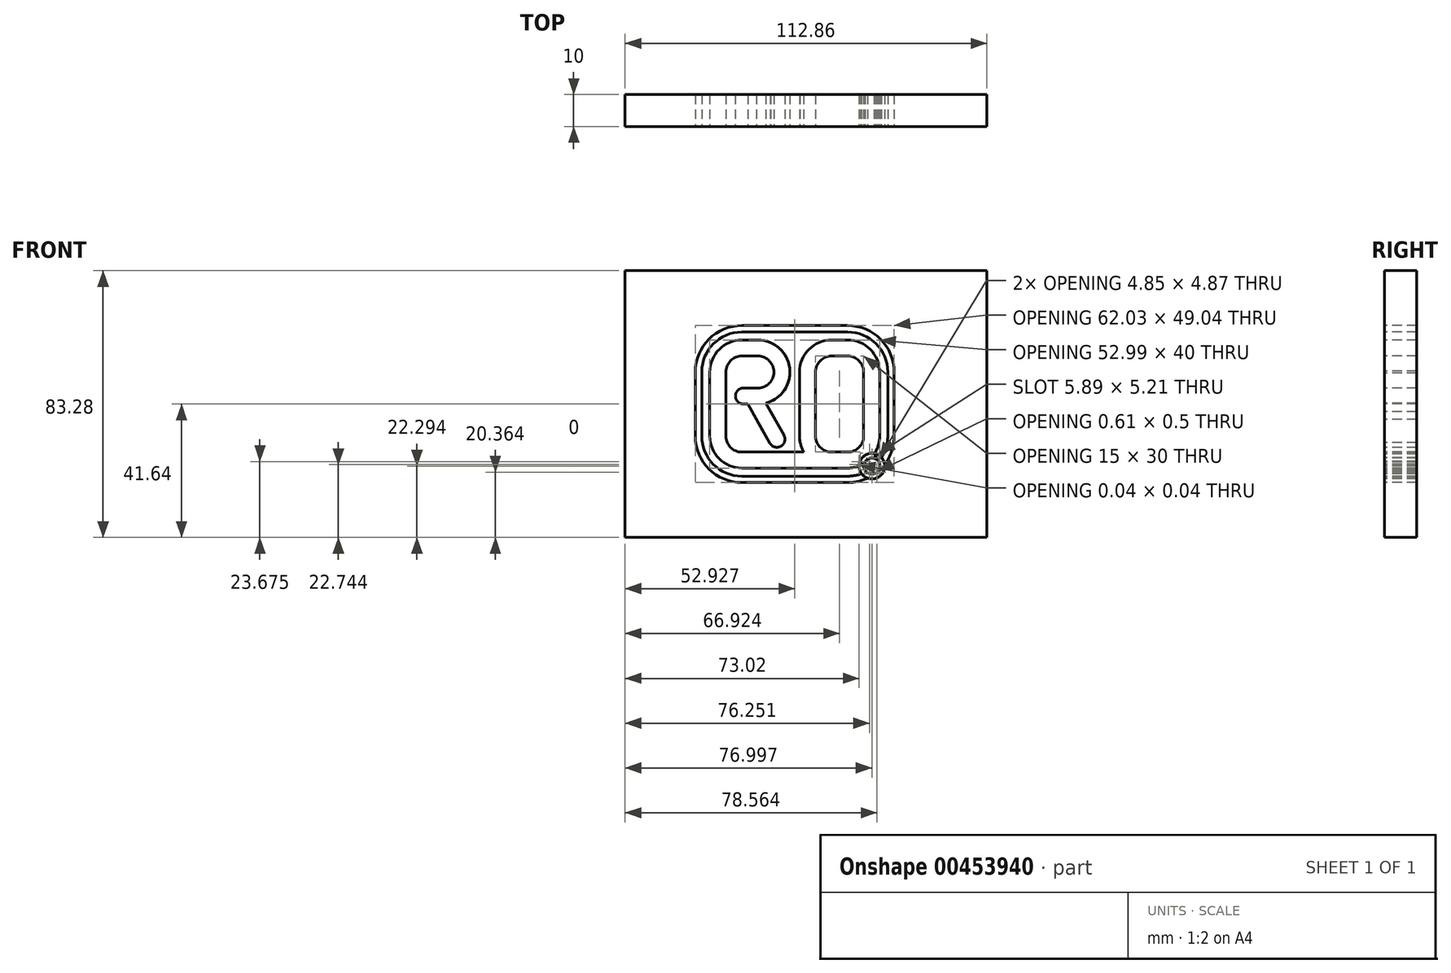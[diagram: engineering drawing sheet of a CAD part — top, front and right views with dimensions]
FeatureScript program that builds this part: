
annotation { "Feature Type Name" : "Feature", "Feature Type Description" : "" }
export const myFeature = defineFeature(function(context is Context, id is Id, definition is map)
    precondition{}
    {
        {
            var Q0;
            Q0=qCreatedBy(makeId("Front.planeOp"),FACE);
            var sketch = newSketch(context, id + "F0", { "sketchPlane" : qUnion([Q0])});
            skPoint(sketch, "E0.middle", {"position": v(0, 0) * mm});
            skLineSegment(sketch, "E1", {"start": v(-25, 10) * mm, "end": v(-25, -10) * mm});
            skLineSegment(sketch, "E2", {"start": v(-2, -20) * mm, "end": v(-0.38, -20) * mm});
            skLineSegment(sketch, "E3", {"start": v(-2, -11) * mm, "end": v(-2, 10) * mm});
            skLineSegment(sketch, "E4", {"start": v(8, 20) * mm, "end": v(13, 20) * mm});
            skLineSegment(sketch, "E5", {"start": v(23, 10) * mm, "end": v(23, -10) * mm});
            skLineSegment(sketch, "E6", {"start": v(13, -20) * mm, "end": v(9, -20) * mm});
            skLineSegment(sketch, "E7", {"start": v(-25, 20) * mm, "end": v(-15, 20) * mm});
            skLineSegment(sketch, "E8", {"start": v(-19.5, 0) * mm, "end": v(-15, 0) * mm});
            skLineSegment(sketch, "E9", {"start": v(-5, 10.33) * mm, "end": v(-5, 10.33) * mm});
            skPoint(sketch, "E10.visualSharp", {"position": v(-5.33, 20) * mm});
            skArc(sketch, "E10.filletArc", {"start": v(-5, 10.33) * mm, "mid": v(-8.05, 17.19) * mm, "end": v(-15, 20) * mm});
            skArc(sketch, "E11.filletArc", {"start": v(-15, 0) * mm, "mid": v(-7.81, 3.05) * mm, "end": v(-5, 10.33) * mm});
            skPoint(sketch, "E12.visualSharp", {"position": v(-3.63, -20) * mm});
            skPoint(sketch, "E13.visualSharp", {"position": v(23, -20) * mm});
            skPoint(sketch, "E14.visualSharp", {"position": v(23, 20) * mm});
            skArc(sketch, "E14.filletArc", {"start": v(23, 10) * mm, "mid": v(20.07, 17.07) * mm, "end": v(13, 20) * mm});
            skPoint(sketch, "E15.visualSharp", {"position": v(-2, 20) * mm});
            skArc(sketch, "E15.filletArc", {"start": v(8, 20) * mm, "mid": v(0.92, 17.07) * mm, "end": v(-2, 10) * mm});
            skPoint(sketch, "E16.visualSharp", {"position": v(-2, -20) * mm});
            skArc(sketch, "E17.0", {"start": v(8, 15) * mm, "mid": v(4.46, 13.54) * mm, "end": v(3, 10) * mm});
            skLineSegment(sketch, "E17.1", {"start": v(3, -11) * mm, "end": v(3, 10) * mm});
            skLineSegment(sketch, "E17.2", {"start": v(8, 15) * mm, "end": v(13, 15) * mm});
            skArc(sketch, "E17.4", {"start": v(18, 10) * mm, "mid": v(16.53, 13.54) * mm, "end": v(13, 15) * mm});
            skLineSegment(sketch, "E17.5", {"start": v(18, 10) * mm, "end": v(18, -10) * mm});
            skArc(sketch, "E17.6", {"start": v(16.57, -18.88) * mm, "mid": v(16.59, -18.88) * mm, "end": v(16.6, -18.87) * mm});
            skLineSegment(sketch, "E17.7", {"start": v(13, -15) * mm, "end": v(9, -15) * mm});
            skArc(sketch, "E18.1", {"start": v(-15, 5) * mm, "mid": v(-11.44, 6.5) * mm, "end": v(-10, 10.08) * mm});
            skArc(sketch, "E18.2", {"start": v(-10, 10.08) * mm, "mid": v(-11.5, 13.56) * mm, "end": v(-15, 15) * mm});
            skLineSegment(sketch, "E18.3", {"start": v(-20, 15) * mm, "end": v(-15, 15) * mm});
            skLineSegment(sketch, "E19.0", {"start": v(-30, 17.5) * mm, "end": v(-30, -10) * mm});
            skLineSegment(sketch, "E20.0", {"start": v(-1, -15) * mm, "end": v(-0.38, -15) * mm});
            skLineSegment(sketch, "E21", {"start": v(-20, -20) * mm, "end": v(-2, -20) * mm});
            skLineSegment(sketch, "E22", {"start": v(-1, -15) * mm, "end": v(0, -15) * mm});
            skLineSegment(sketch, "E23.0", {"start": v(-20, -15) * mm, "end": v(0, -15) * mm});
            skLineSegment(sketch, "E24", {"start": v(-5, 10.33) * mm, "end": v(-5, 0) * mm});
            skLineSegment(sketch, "E25", {"start": v(0.5, -13.5) * mm, "end": v(0.5, -13.5) * mm});
            skPoint(sketch, "E26.visualSharp", {"position": v(3, -13.5) * mm});
            skArc(sketch, "E26.filletArc", {"start": v(0.5, -13.5) * mm, "mid": v(2.26, -12.77) * mm, "end": v(3, -11) * mm, "construction": true});
            skPoint(sketch, "E27.newPointB", {"position": v(-23.5, -13.5) * mm});
            skArc(sketch, "E27.filletArc", {"start": v(-2, -11) * mm, "mid": v(-1.27, -12.77) * mm, "end": v(0.5, -13.5) * mm});
            skPoint(sketch, "E28.visualSharp", {"position": v(-30, -20) * mm});
            skArc(sketch, "E28.filletArc", {"start": v(-30, -19.5) * mm, "mid": v(-29.85, -19.85) * mm, "end": v(-29.5, -20) * mm});
            skLineSegment(sketch, "E29", {"start": v(-7.28, -12.77) * mm, "end": v(-7.28, -12.77) * mm});
            skArc(sketch, "E30.filletArc", {"start": v(-7.28, -12.77) * mm, "mid": v(-6.55, -11) * mm, "end": v(-7.27, -9.24) * mm});
            skArc(sketch, "E31.filletArc", {"start": v(-11.23, -12.21) * mm, "mid": v(-9.4, -13.48) * mm, "end": v(-7.28, -12.77) * mm});
            skLineSegment(sketch, "E32.0", {"start": v(16.6, -18.92) * mm, "end": v(16.57, -18.88) * mm});
            skPoint(sketch, "E33.newPointB", {"position": v(-25, 20) * mm});
            skPoint(sketch, "E34.visualSharp", {"position": v(-23.5, 5) * mm});
            skPoint(sketch, "E35.visualSharp", {"position": v(-23.5, 0) * mm});
            skLineSegment(sketch, "E36", {"start": v(-30, 10) * mm, "end": v(-30, 17.5) * mm});
            skLineSegment(sketch, "E37", {"start": v(-20, 20) * mm, "end": v(-25, 20) * mm});
            skPoint(sketch, "E38.visualSharp", {"position": v(-30, 20) * mm});
            skArc(sketch, "E38.filletArc", {"start": v(-20, 20) * mm, "mid": v(-27.07, 17.07) * mm, "end": v(-30, 10) * mm});
            skPoint(sketch, "E39", {"position": v(21.88, -21.66) * mm});
            skPoint(sketch, "E40.orphan", {"position": v(19.27, -17.06) * mm});
            skLineSegment(sketch, "E41.trimOffspring", {"start": v(13, -20) * mm, "end": v(-0.38, -20) * mm});
            skPoint(sketch, "E42.newPointB", {"position": v(-25, -20) * mm});
            skArc(sketch, "E42.filletArc", {"start": v(-25, -10) * mm, "mid": v(-23.54, -13.54) * mm, "end": v(-20, -15) * mm});
            skLineSegment(sketch, "E43", {"start": v(-15, 20) * mm, "end": v(8, 20) * mm});
            skLineSegment(sketch, "E44", {"start": v(21.86, -24.52) * mm, "end": v(-20, -24.52) * mm});
            skLineSegment(sketch, "E45", {"start": v(27.51, -22.02) * mm, "end": v(27.51, -18.86) * mm});
            skLineSegment(sketch, "E46", {"start": v(13, 24.52) * mm, "end": v(-20, 24.52) * mm});
            skLineSegment(sketch, "E47", {"start": v(-34.52, -10) * mm, "end": v(-34.52, 10) * mm});
            skPoint(sketch, "E48.orphan", {"position": v(19.71, -22.03) * mm});
            skPoint(sketch, "E49.orphan", {"position": v(15.63, -17.94) * mm});
            skArc(sketch, "E50.0", {"start": v(27.51, 10) * mm, "mid": v(23.26, 20.27) * mm, "end": v(13, 24.52) * mm});
            skArc(sketch, "E51.0", {"start": v(25.51, 10) * mm, "mid": v(21.85, 18.85) * mm, "end": v(13, 22.52) * mm});
            skLineSegment(sketch, "E52.0", {"start": v(25.51, -22.07) * mm, "end": v(25.51, -18.99) * mm});
            skLineSegment(sketch, "E53.0", {"start": v(25.02, -22.52) * mm, "end": v(21.98, -22.52) * mm});
            skLineSegment(sketch, "E54.0", {"start": v(-32.52, -10) * mm, "end": v(-32.52, 10) * mm});
            skLineSegment(sketch, "E55.0", {"start": v(13, 22.52) * mm, "end": v(-20, 22.52) * mm});
            skPoint(sketch, "E56.visualSharp", {"position": v(-32.52, 22.52) * mm});
            skArc(sketch, "E56.filletArc", {"start": v(-20, 22.52) * mm, "mid": v(-28.85, 18.85) * mm, "end": v(-32.52, 10) * mm});
            skArc(sketch, "E57.0", {"start": v(-20, 24.52) * mm, "mid": v(-30.27, 20.27) * mm, "end": v(-34.52, 10) * mm});
            skPoint(sketch, "E58.visualSharp", {"position": v(-32.52, -22.52) * mm});
            skLineSegment(sketch, "E59", {"start": v(26.51, -15) * mm, "end": v(26.51, -16.32) * mm});
            skLineSegment(sketch, "E60.0", {"start": v(18.1, -20.77) * mm, "end": v(22.19, -24.85) * mm, "construction": true});
            skLineSegment(sketch, "E61.0", {"start": v(23.76, -15.1) * mm, "end": v(27.84, -19.2) * mm, "construction": true});
            skLineSegment(sketch, "E62.trimOffspring", {"start": v(25.51, -14) * mm, "end": v(25.51, 10) * mm});
            skLineSegment(sketch, "E63.trimOffspring", {"start": v(27.51, -14) * mm, "end": v(27.51, 33) * mm});
            skLineSegment(sketch, "E64.trimOffspring", {"start": v(18.13, -22.52) * mm, "end": v(-20, -22.52) * mm});
            skLineSegment(sketch, "E65", {"start": v(21.86, -24.52) * mm, "end": v(25.02, -24.52) * mm});
            skLineSegment(sketch, "E66", {"start": v(27.51, -14) * mm, "end": v(27.51, -22.02) * mm});
            skLineSegment(sketch, "E67.bottom", {"start": v(-56.43, 41.64) * mm, "end": v(56.43, 41.64) * mm});
            skLineSegment(sketch, "E67.top", {"start": v(-56.43, -41.64) * mm, "end": v(56.43, -41.64) * mm});
            skLineSegment(sketch, "E67.left", {"start": v(-56.43, 41.64) * mm, "end": v(-56.43, -41.64) * mm});
            skLineSegment(sketch, "E67.right", {"start": v(56.43, 41.64) * mm, "end": v(56.43, -41.64) * mm});
            skLineSegment(sketch, "E68", {"start": v(0, 0) * mm, "end": v(0, -38.7) * mm, "construction": true});
            skLineSegment(sketch, "E69", {"start": v(0, 0) * mm, "end": v(33.56, 0) * mm, "construction": true});
            skArc(sketch, "E70.filletArc", {"start": v(-20, 15) * mm, "mid": v(-23.54, 13.54) * mm, "end": v(-25, 10) * mm});
            skArc(sketch, "E71.0", {"start": v(-30, -10) * mm, "mid": v(-27.07, -17.07) * mm, "end": v(-20, -20) * mm});
            skArc(sketch, "E72.0", {"start": v(-34.52, -10) * mm, "mid": v(-30.27, -20.27) * mm, "end": v(-20, -24.52) * mm});
            skArc(sketch, "E73.0", {"start": v(-32.52, -10) * mm, "mid": v(-28.85, -18.85) * mm, "end": v(-20, -22.52) * mm});
            skLineSegment(sketch, "E74", {"start": v(-15, 5) * mm, "end": v(-19.5, 5) * mm});
            skLineSegment(sketch, "E75", {"start": v(-23.5, 2.5) * mm, "end": v(-23.5, 2.5) * mm});
            skArc(sketch, "E76.filletArc", {"start": v(-21, 5) * mm, "mid": v(-22.77, 4.27) * mm, "end": v(-23.5, 2.5) * mm, "construction": true});
            skArc(sketch, "E77.filletArc", {"start": v(-23.5, 2.5) * mm, "mid": v(-22.77, 0.73) * mm, "end": v(-21, 0) * mm, "construction": true});
            skPoint(sketch, "E78.startSnap0", {"position": v(-6.55, -11) * mm});
            skLineSegment(sketch, "E79", {"start": v(-22.87, 0.84) * mm, "end": v(-10.92, -12.66) * mm, "construction": true});
            skLineSegment(sketch, "E80.0", {"start": v(-19.13, 4.16) * mm, "end": v(-7.17, -9.34) * mm, "construction": true});
            skArc(sketch, "E81.0", {"start": v(13, -22.52) * mm, "mid": v(15.21, -22.32) * mm, "end": v(17.36, -21.73) * mm});
            skArc(sketch, "E82.0", {"start": v(13, -24.52) * mm, "mid": v(16.18, -24.17) * mm, "end": v(19.22, -23.12) * mm});
            skCircle(sketch, "E83", {"center": v(20.58, -19.36) * mm, "radius": 2.5 * mm});
            skLineSegment(sketch, "E84", {"start": v(-21, 5) * mm, "end": v(-21, 0) * mm, "construction": true});
            skLineSegment(sketch, "E85", {"start": v(-21, 5) * mm, "end": v(-18.16, 0) * mm});
            skLineSegment(sketch, "E86.0", {"start": v(-16.65, 7.47) * mm, "end": v(-12.58, 0.3) * mm});
            skLineSegment(sketch, "E87", {"start": v(-22, 7.3) * mm, "end": v(-22, -4.59) * mm});
            skLineSegment(sketch, "E88", {"start": v(-28.56, 2.5) * mm, "end": v(-6.16, 2.5) * mm, "construction": true});
            skCircle(sketch, "E89", {"center": v(-19.5, 2.5) * mm, "radius": 2.5 * mm});
            skArc(sketch, "E90.0", {"start": v(16.6, -18.87) * mm, "mid": v(16.6, -18.9) * mm, "end": v(16.6, -18.92) * mm});
            skLineSegment(sketch, "E91", {"start": v(10.5, 15) * mm, "end": v(10.5, 5.39) * mm, "construction": true});
            skArc(sketch, "E92.MirrorCS", {"start": v(8, -15) * mm, "mid": v(4.46, -13.54) * mm, "end": v(3, -10) * mm});
            skArc(sketch, "E93.MirrorCS", {"start": v(8, -20) * mm, "mid": v(0.92, -17.07) * mm, "end": v(-2, -10) * mm});
            skLineSegment(sketch, "E94.trimOffspring", {"start": v(8, -15) * mm, "end": v(9, -15) * mm});
            skArc(sketch, "E95", {"start": v(12.04, -20) * mm, "mid": v(14.54, -17.5) * mm, "end": v(12.04, -15) * mm});
            skArc(sketch, "E96", {"start": v(18, -4.59) * mm, "mid": v(20.5, -7.09) * mm, "end": v(23, -4.59) * mm});
            skArc(sketch, "E97", {"start": v(15.38, -14.4) * mm, "mid": v(18.74, -13.52) * mm, "end": v(18, -10.13) * mm});
            skLineSegment(sketch, "E98", {"start": v(-11.07, -2.36) * mm, "end": v(-15.42, -4.83) * mm});
            skArc(sketch, "E99", {"start": v(-10.92, -2.63) * mm, "mid": v(-14.33, -1.7) * mm, "end": v(-15.27, -5.1) * mm});
            skLineSegment(sketch, "E100.trimOffspring", {"start": v(-11.07, -2.36) * mm, "end": v(-6.74, -10) * mm});
            skLineSegment(sketch, "E101.trimOffspring", {"start": v(-15.42, -4.83) * mm, "end": v(-11.1, -12.46) * mm});
            skLineSegment(sketch, "E102", {"start": v(21.83, -21.52) * mm, "end": v(16.99, -13) * mm, "construction": true});
            skLineSegment(sketch, "E103", {"start": v(18.8, -11) * mm, "end": v(22.76, -18.14) * mm});
            skLineSegment(sketch, "E104", {"start": v(15.05, -14.56) * mm, "end": v(18.4, -20.57) * mm});
            skLineSegment(sketch, "E105", {"start": v(-11.07, -2.36) * mm, "end": v(-13.75, 2.35) * mm});
            skArc(sketch, "E106.MirrorCS", {"start": v(13, -15) * mm, "mid": v(16.53, -13.54) * mm, "end": v(18, -10) * mm});
            skArc(sketch, "E107.MirrorCS", {"start": v(13, -20) * mm, "mid": v(14.82, -19.83) * mm, "end": v(16.58, -19.34) * mm});
            skLineSegment(sketch, "E108", {"start": v(-15.42, -4.83) * mm, "end": v(-18.16, 0) * mm});
            skArc(sketch, "E109.0", {"start": v(24.54, -18.8) * mm, "mid": v(24.21, -17.68) * mm, "end": v(23.57, -16.7) * mm});
            skArc(sketch, "E110.trimOffspring", {"start": v(17.36, -21.73) * mm, "mid": v(18.19, -22.56) * mm, "end": v(19.22, -23.12) * mm});
            skArc(sketch, "E111.trimOffspring", {"start": v(21.39, -15.44) * mm, "mid": v(21.32, -15.43) * mm, "end": v(21.25, -15.41) * mm});
            skArc(sketch, "E112.trimOffspring", {"start": v(16.88, -17.84) * mm, "mid": v(16.66, -18.58) * mm, "end": v(16.58, -19.34) * mm});
            skArc(sketch, "E113.trimOffspring", {"start": v(24.54, -18.8) * mm, "mid": v(26.75, -14.65) * mm, "end": v(27.51, -10) * mm});
            skArc(sketch, "E114.trimOffspring", {"start": v(23.57, -16.7) * mm, "mid": v(25.02, -13.49) * mm, "end": v(25.51, -10) * mm});
            skArc(sketch, "E115.trimOffspring", {"start": v(18.56, -21.22) * mm, "mid": v(20.78, -19.8) * mm, "end": v(22.66, -17.96) * mm});
            skArc(sketch, "E116.trimOffspring", {"start": v(20.04, -22.7) * mm, "mid": v(21.28, -21.92) * mm, "end": v(22.44, -21.03) * mm});
            skCircle(sketch, "E117.0", {"center": v(20.58, -19.36) * mm, "radius": 4 * mm});
            skArc(sketch, "E118.trimOffspring", {"start": v(21.32, -15.54) * mm, "mid": v(22.57, -12.9) * mm, "end": v(23, -10) * mm});
            skArc(sketch, "E119.trimOffspring", {"start": v(18.22, -18.52) * mm, "mid": v(19.3, -17.77) * mm, "end": v(20.25, -16.88) * mm});
            skSolve(sketch);
        }
        {
            var Q0;
            Q0=makeQuery(id+"F0.imprint","IMPRINT",FACE,{"disambiguationData":[TD([[makeQuery(id+"F0.imprint","IMPRINT",EDGE,{"derivedFrom":sQuery(id+"F0.wireOp",EDGE,"E1")}),-1.0]])]});
            var Q1;
            {var subQ6=sQuery(id+"F0.wireOp",EDGE,"8dgEX87s-OnN3-UPAw-RyUf-tcfM0RuKeMZf");Q1=makeQuery(id+"F0.imprint","IMPRINT",FACE,{"disambiguationData":[TD([[makeQuery(id+"F0.imprint","IMPRINT",EDGE,{"derivedFrom":subQ6}),1.0]])]});}
            var Q2;
            {var subQ0=sQuery(id+"F0.wireOp",EDGE,"S70SFG3v-wlmV-iE8w-7gkR-MiBzXbBwRlH9");var subQ1=makeQuery(id+"F0.imprint","INTERSECT",VERTEX,{"derivedFrom":[sQuery(id+"F0.wireOp",EDGE,"c0c087a9-fd36-4214-a694-875f0f01d769.0"),subQ0]});Q2=makeQuery(id+"F0.imprint","IMPRINT",FACE,{"disambiguationData":[TD([[makeQuery(id+"F0.imprint","IMPRINT",EDGE,{"disambiguationData":[TD([[subQ1,-1.0]])],"derivedFrom":subQ0}),1.0]])]});}
            var Q3;
            {var subQ1=sQuery(id+"F0.wireOp",EDGE,"c0c087a9-fd36-4214-a694-875f0f01d769.0");Q3=makeQuery(id+"F0.imprint","IMPRINT",FACE,{"disambiguationData":[TD([[makeQuery(id+"F0.imprint","IMPRINT",EDGE,{"derivedFrom":subQ1}),-1.0]])]});}
            var Q4;
            {var subQ0=sQuery(id+"F0.wireOp",EDGE,"E0.bottom");Q4=makeQuery(id+"F0.imprint","IMPRINT",FACE,{"disambiguationData":[TD([[makeQuery(id+"F0.imprint","IMPRINT",EDGE,{"derivedFrom":subQ0}),-1.0]])]});}
            var Q5;
            {var subQ0=sQuery(id+"F0.wireOp",EDGE,"E0.bottom");Q5=makeQuery(id+"F0.imprint","IMPRINT",FACE,{"disambiguationData":[TD([[makeQuery(id+"F0.imprint","IMPRINT",EDGE,{"derivedFrom":subQ0}),1.0]])]});}
            var Q6;
            {var subQ3=sQuery(id+"F0.wireOp",EDGE,"E8");var subQ7=sQuery(id+"F0.wireOp",EDGE,"E11.filletArc");var subQ8=makeQuery(id+"F0.imprint","INTERSECT",VERTEX,{"derivedFrom":[subQ3,subQ7]});Q6=makeQuery(id+"F0.imprint","IMPRINT",FACE,{"disambiguationData":[TD([[makeQuery(id+"F0.imprint","IMPRINT",EDGE,{"disambiguationData":[TD([[subQ8,1.0]])],"derivedFrom":subQ3}),1.0]])]});}
            var Q7;
            {var subQ4=sQuery(id+"F0.wireOp",EDGE,"E76.filletArc");Q7=makeQuery(id+"F0.imprint","IMPRINT",FACE,{"disambiguationData":[TD([[makeQuery(id+"F0.imprint","IMPRINT",EDGE,{"derivedFrom":subQ4}),1.0]])]});}
            var Q8;
            {var subQ0=sQuery(id+"F0.wireOp",EDGE,"E31.filletArc");Q8=makeQuery(id+"F0.imprint","IMPRINT",FACE,{"disambiguationData":[TD([[makeQuery(id+"F0.imprint","IMPRINT",EDGE,{"derivedFrom":subQ0}),1.0]])]});}
            var Q9;
            Q9=makeQuery(id+"F0.imprint","IMPRINT",FACE,{"disambiguationData":[TD([[makeQuery(id+"F0.imprint","IMPRINT",EDGE,{"derivedFrom":sQuery(id+"F0.wireOp",EDGE,"E83")}),1.0]])]});
            var Q10;
            {var subQ0=sQuery(id+"F0.wireOp",EDGE,"E88");var subQ1=sQuery(id+"F0.wireOp",EDGE,"E11.filletArc");var subQ2=makeQuery(id+"F0.imprint","INTERSECT",VERTEX,{"derivedFrom":[subQ1,subQ0]});Q10=makeQuery(id+"F0.imprint","IMPRINT",FACE,{"disambiguationData":[TD([[makeQuery(id+"F0.imprint","IMPRINT",EDGE,{"disambiguationData":[TD([[subQ2,1.0]])],"derivedFrom":subQ1}),1.0]])]});}
            var Q11;
            {var subQ0=sQuery(id+"F0.wireOp",EDGE,"E89");var subQ1=sQuery(id+"F0.wireOp",EDGE,"E74");var subQ2=makeQuery(id+"F0.imprint","INTERSECT",VERTEX,{"derivedFrom":[subQ1,subQ0]});Q11=makeQuery(id+"F0.imprint","IMPRINT",FACE,{"disambiguationData":[TD([[makeQuery(id+"F0.imprint","IMPRINT",EDGE,{"disambiguationData":[TD([[subQ2,1.0]])],"derivedFrom":subQ1}),1.0]])]});}
            var Q12;
            {var subQ0=sQuery(id+"F0.wireOp",EDGE,"E88");var subQ1=sQuery(id+"F0.wireOp",EDGE,"E85");var subQ2=makeQuery(id+"F0.imprint","INTERSECT",VERTEX,{"derivedFrom":[subQ1,subQ0]});Q12=makeQuery(id+"F0.imprint","IMPRINT",FACE,{"disambiguationData":[TD([[makeQuery(id+"F0.imprint","IMPRINT",EDGE,{"disambiguationData":[TD([[subQ2,-1.0]])],"derivedFrom":subQ1}),-1.0]])]});}
            var Q13;
            {var subQ0=sQuery(id+"F0.wireOp",EDGE,"E89");var subQ1=sQuery(id+"F0.wireOp",EDGE,"E85");var subQ2=makeQuery(id+"F0.imprint","INTERSECT",VERTEX,{"disambiguationData":[OD(0.0)],"derivedFrom":[subQ1,subQ0]});Q13=makeQuery(id+"F0.imprint","IMPRINT",FACE,{"disambiguationData":[TD([[makeQuery(id+"F0.imprint","IMPRINT",EDGE,{"disambiguationData":[TD([[subQ2,-1.0]])],"derivedFrom":subQ1}),-1.0]])]});}
            var Q14;
            {var subQ0=sQuery(id+"F0.wireOp",EDGE,"E89");var subQ1=sQuery(id+"F0.wireOp",EDGE,"E85");var subQ2=makeQuery(id+"F0.imprint","INTERSECT",VERTEX,{"disambiguationData":[OD(0.0)],"derivedFrom":[subQ1,subQ0]});Q14=makeQuery(id+"F0.imprint","IMPRINT",FACE,{"disambiguationData":[TD([[makeQuery(id+"F0.imprint","IMPRINT",EDGE,{"disambiguationData":[TD([[subQ2,-1.0]])],"derivedFrom":subQ1}),1.0]])]});}
            var Q15;
            {var subQ0=sQuery(id+"F0.wireOp",EDGE,"E88");var subQ1=sQuery(id+"F0.wireOp",EDGE,"E85");var subQ2=makeQuery(id+"F0.imprint","INTERSECT",VERTEX,{"derivedFrom":[subQ1,subQ0]});Q15=makeQuery(id+"F0.imprint","IMPRINT",FACE,{"disambiguationData":[TD([[makeQuery(id+"F0.imprint","IMPRINT",EDGE,{"disambiguationData":[TD([[subQ2,-1.0]])],"derivedFrom":subQ1}),1.0]])]});}
            var Q16;
            {var subQ0=sQuery(id+"F0.wireOp",EDGE,"E89");var subQ1=sQuery(id+"F0.wireOp",EDGE,"E8");var subQ2=makeQuery(id+"F0.imprint","INTERSECT",VERTEX,{"derivedFrom":[subQ1,subQ0]});Q16=makeQuery(id+"F0.imprint","IMPRINT",FACE,{"disambiguationData":[TD([[makeQuery(id+"F0.imprint","IMPRINT",EDGE,{"disambiguationData":[TD([[subQ2,-1.0]])],"derivedFrom":subQ1}),1.0]])]});}
            var Q17;
            Q17=makeQuery(id+"F0.imprint","IMPRINT",FACE,{"disambiguationData":[TD([[makeQuery(id+"F0.imprint","IMPRINT",EDGE,{"derivedFrom":sQuery(id+"F0.wireOp",EDGE,"E4")}),-1.0]])]});
            var Q18;
            {var subQ0=sQuery(id+"F0.wireOp",EDGE,"E97");var subQ1=sQuery(id+"F0.wireOp",EDGE,"l3Agq5ap-yWmA-VVue-g4vt-Hq9HFho2LNEB");var subQ2=makeQuery(id+"F0.imprint","INTERSECT",VERTEX,{"disambiguationData":[OD(0.0)],"derivedFrom":[subQ1,subQ0]});Q18=makeQuery(id+"F0.imprint","IMPRINT",FACE,{"disambiguationData":[TD([[makeQuery(id+"F0.imprint","IMPRINT",EDGE,{"disambiguationData":[TD([[subQ2,1.0]])],"derivedFrom":subQ1}),-1.0]])]});}
            var Q19;
            {var subQ0=sQuery(id+"F0.wireOp",EDGE,"E97");var subQ1=sQuery(id+"F0.wireOp",EDGE,"l3Agq5ap-yWmA-VVue-g4vt-Hq9HFho2LNEB");var subQ2=makeQuery(id+"F0.imprint","INTERSECT",VERTEX,{"disambiguationData":[OD(0.0)],"derivedFrom":[subQ1,subQ0]});Q19=makeQuery(id+"F0.imprint","IMPRINT",FACE,{"disambiguationData":[TD([[makeQuery(id+"F0.imprint","IMPRINT",EDGE,{"disambiguationData":[TD([[subQ2,1.0]])],"derivedFrom":subQ1}),1.0]])]});}
            var Q20;
            {var subQ0=sQuery(id+"F0.wireOp",EDGE,"m8UYtWHv-qO4X-QN6X-iKXV-4yPTMy5MIqK1");Q20=makeQuery(id+"F0.imprint","IMPRINT",FACE,{"disambiguationData":[TD([[makeQuery(id+"F0.imprint","IMPRINT",EDGE,{"derivedFrom":subQ0}),-1.0]])]});}
            var Q21;
            {var subQ4=sQuery(id+"F0.wireOp",EDGE,"GEM00Yna-KXC5-UJpv-niI3-6qlbkwYTooAT");Q21=makeQuery(id+"F0.imprint","IMPRINT",FACE,{"disambiguationData":[TD([[makeQuery(id+"F0.imprint","IMPRINT",EDGE,{"derivedFrom":subQ4}),1.0]])]});}
            var Q22;
            {var subQ0=sQuery(id+"F0.wireOp",EDGE,"E99");var subQ1=sQuery(id+"F0.wireOp",EDGE,"E98");var subQ2=makeQuery(id+"F0.imprint","INTERSECT",VERTEX,{"disambiguationData":[OD(0.0)],"derivedFrom":[subQ1,subQ0]});Q22=makeQuery(id+"F0.imprint","IMPRINT",FACE,{"disambiguationData":[TD([[makeQuery(id+"F0.imprint","IMPRINT",EDGE,{"disambiguationData":[TD([[subQ2,-1.0]])],"derivedFrom":subQ1}),-1.0]])]});}
            var Q23;
            {var subQ6=sQuery(id+"F0.wireOp",EDGE,"E104");Q23=makeQuery(id+"F0.imprint","IMPRINT",FACE,{"disambiguationData":[TD([[makeQuery(id+"F0.imprint","IMPRINT",EDGE,{"derivedFrom":subQ6}),1.0]])]});}
            var Q24;
            {var subQ0=sQuery(id+"F0.wireOp",EDGE,"E97");var subQ1=makeQuery(id+"F0.imprint","INTERSECT",VERTEX,{"derivedFrom":[subQ0,sQuery(id+"F0.wireOp",EDGE,"E103")]});Q24=makeQuery(id+"F0.imprint","IMPRINT",FACE,{"disambiguationData":[TD([[makeQuery(id+"F0.imprint","IMPRINT",EDGE,{"disambiguationData":[TD([[subQ1,-1.0]])],"derivedFrom":subQ0}),1.0]])]});}
            var Q25;
            {var subQ5=sQuery(id+"F0.wireOp",EDGE,"E96");Q25=makeQuery(id+"F0.imprint","IMPRINT",FACE,{"disambiguationData":[TD([[makeQuery(id+"F0.imprint","IMPRINT",EDGE,{"derivedFrom":subQ5}),-1.0]])]});}
            var Q26;
            {var subQ0=sQuery(id+"F0.wireOp",EDGE,"E108");Q26=makeQuery(id+"F0.imprint","IMPRINT",FACE,{"disambiguationData":[TD([[makeQuery(id+"F0.imprint","IMPRINT",EDGE,{"derivedFrom":subQ0}),-1.0]])]});}
            var Q27;
            {var subQ8=sQuery(id+"F0.wireOp",EDGE,"E17.6");Q27=makeQuery(id+"F0.imprint","IMPRINT",FACE,{"disambiguationData":[TD([[makeQuery(id+"F0.imprint","IMPRINT",EDGE,{"derivedFrom":subQ8}),1.0]])]});}
            var Q28;
            {var subQ0=sQuery(id+"F0.wireOp",EDGE,"E112.trimOffspring");var subQ5=sQuery(id+"F0.wireOp",EDGE,"E104");var subQ7=makeQuery(id+"F0.imprint","INTERSECT",VERTEX,{"derivedFrom":[subQ5,subQ0]});Q28=makeQuery(id+"F0.imprint","IMPRINT",FACE,{"disambiguationData":[TD([[makeQuery(id+"F0.imprint","IMPRINT",EDGE,{"disambiguationData":[TD([[subQ7,-1.0]])],"derivedFrom":subQ5}),-1.0]])]});}
            var Q29;
            {var subQ0=sQuery(id+"F0.wireOp",EDGE,"E107.MirrorCS");var subQ1=sQuery(id+"F0.wireOp",EDGE,"E83");var subQ2=makeQuery(id+"F0.imprint","INTERSECT",VERTEX,{"disambiguationData":[OD(0.0)],"derivedFrom":[subQ1,subQ0]});Q29=makeQuery(id+"F0.imprint","IMPRINT",FACE,{"disambiguationData":[TD([[makeQuery(id+"F0.imprint","IMPRINT",EDGE,{"disambiguationData":[TD([[subQ2,-1.0]])],"derivedFrom":subQ1}),1.0]])]});}
            var Q30;
            {var subQ0=sQuery(id+"F0.wireOp",EDGE,"E111.trimOffspring");Q30=makeQuery(id+"F0.imprint","IMPRINT",FACE,{"disambiguationData":[TD([[makeQuery(id+"F0.imprint","IMPRINT",EDGE,{"derivedFrom":subQ0}),1.0]])]});}
            var Q31;
            {var subQ0=sQuery(id+"F0.wireOp",EDGE,"E119.trimOffspring");Q31=makeQuery(id+"F0.imprint","IMPRINT",FACE,{"disambiguationData":[TD([[makeQuery(id+"F0.imprint","IMPRINT",EDGE,{"derivedFrom":subQ0}),1.0]])]});}
            extrude(context, id + "F1", {"entities" : qUnion([Q0, Q1, Q2, Q3, Q4, Q5, Q6, Q7, Q8, Q9, Q10, Q11, Q12, Q13, Q14, Q15, Q16, Q17, Q18, Q19, Q20, Q21, Q22, Q23, Q24, Q25, Q26, Q27, Q28, Q29, Q30, Q31]), "oppositeDirection" : true, "depth" : 10 * mm});
        }
        {
            var Q0;
            Q0=makeQuery(id+"F0.imprint","IMPRINT",FACE,{"disambiguationData":[TD([[makeQuery(id+"F0.imprint","IMPRINT",EDGE,{"derivedFrom":sQuery(id+"F0.wireOp",EDGE,"E1")}),1.0]])]});
            var Q1;
            {var subQ16=sQuery(id+"F0.wireOp",EDGE,"E2");Q1=makeQuery(id+"F0.imprint","IMPRINT",FACE,{"disambiguationData":[TD([[makeQuery(id+"F0.imprint","IMPRINT",EDGE,{"derivedFrom":subQ16}),-1.0]])]});}
            var Q2;
            {var subQ13=sQuery(id+"F0.wireOp",EDGE,"E17.0");Q2=makeQuery(id+"F0.imprint","IMPRINT",FACE,{"disambiguationData":[TD([[makeQuery(id+"F0.imprint","IMPRINT",EDGE,{"derivedFrom":subQ13}),1.0]])]});}
            var Q3;
            {var subQ0=sQuery(id+"F0.wireOp",EDGE,"E115.trimOffspring");var subQ1=sQuery(id+"F0.wireOp",EDGE,"E83");var subQ2=makeQuery(id+"F0.imprint","INTERSECT",VERTEX,{"disambiguationData":[OD(1.0)],"derivedFrom":[subQ1,subQ0]});Q3=makeQuery(id+"F0.imprint","IMPRINT",FACE,{"disambiguationData":[TD([[makeQuery(id+"F0.imprint","IMPRINT",EDGE,{"disambiguationData":[TD([[subQ2,-1.0]])],"derivedFrom":subQ1}),-1.0]])]});}
            var Q4;
            {var subQ0=sQuery(id+"F0.wireOp",EDGE,"E104");var subQ1=sQuery(id+"F0.wireOp",EDGE,"E83");var subQ2=makeQuery(id+"F0.imprint","INTERSECT",VERTEX,{"derivedFrom":[subQ1,subQ0]});Q4=makeQuery(id+"F0.imprint","IMPRINT",FACE,{"disambiguationData":[TD([[makeQuery(id+"F0.imprint","IMPRINT",EDGE,{"disambiguationData":[TD([[subQ2,1.0]])],"derivedFrom":subQ1}),-1.0]])]});}
            extrude(context, id + "F2", {"entities" : qUnion([Q0, Q1, Q2, Q3, Q4]), "oppositeDirection" : true, "depth" : 10 * mm});
        }
        {
            var Q0;
            Q0=makeQuery(id+"F0.imprint","IMPRINT",FACE,{"disambiguationData":[TD([[makeQuery(id+"F0.imprint","IMPRINT",EDGE,{"derivedFrom":sQuery(id+"F0.wireOp",EDGE,"E46")}),1.0]])]});
            var Q1;
            {var subQ0=sQuery(id+"F0.wireOp",EDGE,"aTrX08yB-o83u-csdW-HvKf-6qn933KxLSEO");var subQ2=makeQuery(id+"F0.imprint","IMPRINT",VERTEX,{"derivedFrom":subQ0});Q1=makeQuery(id+"F0.imprint","IMPRINT",FACE,{"disambiguationData":[TD([[makeQuery(id+"F0.imprint","IMPRINT",EDGE,{"disambiguationData":[TD([[subQ2,-1.0]])],"derivedFrom":subQ0}),1.0]])]});}
            var Q2;
            {var subQ0=sQuery(id+"F0.wireOp",EDGE,"orb3SBHr-i0Mj-h6B2-otKM-5Ab6eh35dINg");var subQ3=makeQuery(id+"F0.imprint","IMPRINT",VERTEX,{"derivedFrom":subQ0});Q2=makeQuery(id+"F0.imprint","IMPRINT",FACE,{"disambiguationData":[TD([[makeQuery(id+"F0.imprint","IMPRINT",EDGE,{"disambiguationData":[TD([[subQ3,1.0]])],"derivedFrom":subQ0}),1.0]])]});}
            var Q3;
            {var subQ3=sQuery(id+"F0.wireOp",EDGE,"E81.0");Q3=makeQuery(id+"F0.imprint","IMPRINT",FACE,{"disambiguationData":[TD([[makeQuery(id+"F0.imprint","IMPRINT",EDGE,{"derivedFrom":subQ3}),-1.0]])]});}
            extrude(context, id + "F3", {"entities" : qUnion([Q0, Q1, Q2, Q3]), "oppositeDirection" : true, "depth" : 10 * mm});
        }
        {
            var Q0;
            Q0=makeQuery(id+"F0.imprint","IMPRINT",FACE,{"disambiguationData":[TD([[makeQuery(id+"F0.imprint","IMPRINT",EDGE,{"derivedFrom":sQuery(id+"F0.wireOp",EDGE,"E46")}),-1.0]])]});
            var Q1;
            {var subQ0=sQuery(id+"F0.wireOp",EDGE,"E117.0");var subQ24=makeQuery(id+"F0.imprint","IMPRINT",VERTEX,{"derivedFrom":subQ0});Q1=makeQuery(id+"F0.imprint","IMPRINT",FACE,{"disambiguationData":[TD([[makeQuery(id+"F0.imprint","IMPRINT",EDGE,{"disambiguationData":[TD([[subQ24,1.0]])],"derivedFrom":subQ0}),1.0]])]});}
            var Q2;
            {var subQ1=sQuery(id+"F0.wireOp",EDGE,"E83");var subQ3=sQuery(id+"F0.wireOp",EDGE,"E119.trimOffspring");var subQ10=makeQuery(id+"F0.imprint","INTERSECT",VERTEX,{"disambiguationData":[OD(1.0)],"derivedFrom":[subQ1,subQ3]});Q2=makeQuery(id+"F0.imprint","IMPRINT",FACE,{"disambiguationData":[TD([[makeQuery(id+"F0.imprint","IMPRINT",EDGE,{"disambiguationData":[TD([[subQ10,1.0]])],"derivedFrom":subQ1}),-1.0]])]});}
            extrude(context, id + "F4", {"entities" : qUnion([Q0, Q1, Q2]), "oppositeDirection" : true, "depth" : 10 * mm});
        }
    });
